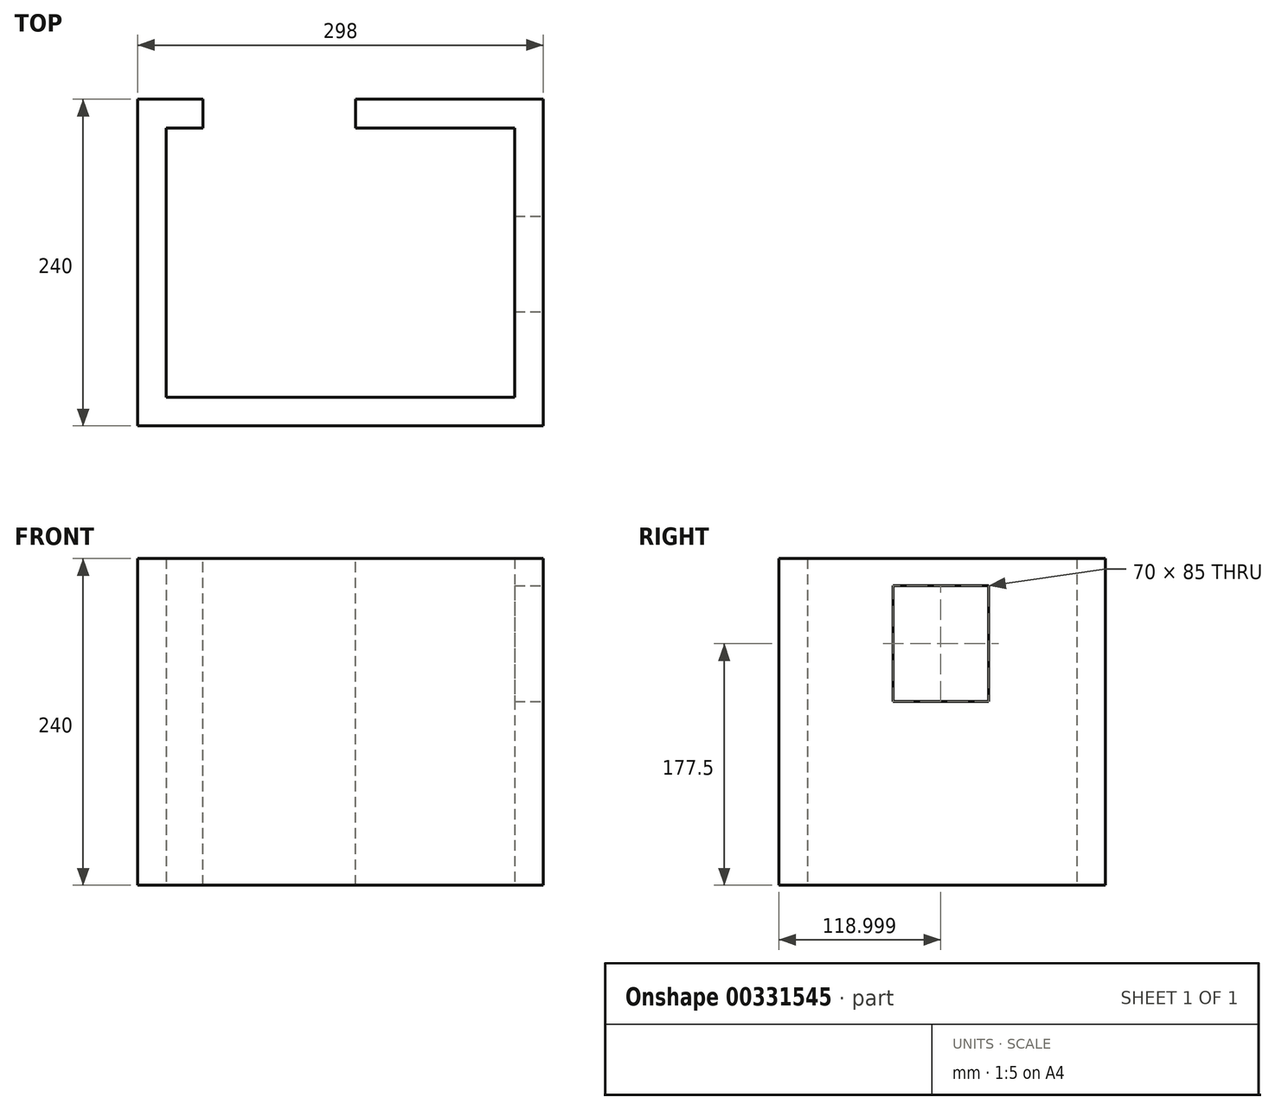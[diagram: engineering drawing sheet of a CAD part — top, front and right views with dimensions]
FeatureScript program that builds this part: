
annotation { "Feature Type Name" : "Feature", "Feature Type Description" : "" }
export const myFeature = defineFeature(function(context is Context, id is Id, definition is map)
    precondition{}
    {
        {
            var Q0;
            Q0=qCreatedBy(makeId("Top.planeOp"),FACE);
            var sketch = newSketch(context, id + "F0", { "sketchPlane" : qUnion([Q0])});
            skLineSegment(sketch, "E0", {"start": v(1313, 440) * mm, "end": v(1313, 406) * mm});
            skLineSegment(sketch, "E1", {"start": v(1313, -267) * mm, "end": v(1313, -301) * mm});
            skLineSegment(sketch, "E2", {"start": v(1313, -301) * mm, "end": v(647, -301) * mm});
            skLineSegment(sketch, "E3", {"start": v(1279, -267) * mm, "end": v(647, -267) * mm});
            skLineSegment(sketch, "E4", {"start": v(1279, 406) * mm, "end": v(688, 406) * mm});
            skLineSegment(sketch, "E5", {"start": v(688, 406) * mm, "end": v(688, -75) * mm});
            skLineSegment(sketch, "E6", {"start": v(688, -75) * mm, "end": v(413, -75) * mm});
            skLineSegment(sketch, "E7", {"start": v(647, -301) * mm, "end": v(647, -267) * mm});
            skLineSegment(sketch, "E8", {"start": v(536, -301) * mm, "end": v(536, -267) * mm});
            skLineSegment(sketch, "E9", {"start": v(536, -267) * mm, "end": v(328, -267) * mm});
            skLineSegment(sketch, "E10", {"start": v(328, -267) * mm, "end": v(328, -407) * mm});
            skLineSegment(sketch, "E11", {"start": v(328, -407) * mm, "end": v(-40, -407) * mm});
            skLineSegment(sketch, "E12", {"start": v(-40, -407) * mm, "end": v(-40, -188) * mm});
            skLineSegment(sketch, "E13", {"start": v(-40, -188) * mm, "end": v(-105, -188) * mm});
            skLineSegment(sketch, "E14", {"start": v(536, -301) * mm, "end": v(362, -301) * mm});
            skLineSegment(sketch, "E15", {"start": v(362, -301) * mm, "end": v(362, -440) * mm});
            skLineSegment(sketch, "E16", {"start": v(-60, -407) * mm, "end": v(-60, -215) * mm});
            skLineSegment(sketch, "E17", {"start": v(-60, -215) * mm, "end": v(-105, -215) * mm});
            skLineSegment(sketch, "E18", {"start": v(-105, -188) * mm, "end": v(-105, -215) * mm});
            skLineSegment(sketch, "E19", {"start": v(-60, -407) * mm, "end": v(-282, -407) * mm});
            skLineSegment(sketch, "E20", {"start": v(-282, -407) * mm, "end": v(-282, -287) * mm});
            skLineSegment(sketch, "E21", {"start": v(-282, -287) * mm, "end": v(-330, -287) * mm});
            skLineSegment(sketch, "E22", {"start": v(-330, -287) * mm, "end": v(-330, -407) * mm});
            skLineSegment(sketch, "E23", {"start": v(-330, -407) * mm, "end": v(-497, -407) * mm});
            skLineSegment(sketch, "E24", {"start": v(-197, -188) * mm, "end": v(-197, -215) * mm});
            skLineSegment(sketch, "E25", {"start": v(-197, -188) * mm, "end": v(-765, -188) * mm});
            skLineSegment(sketch, "E26", {"start": v(-197, -215) * mm, "end": v(-497, -215) * mm});
            skLineSegment(sketch, "E27", {"start": v(-497, -215) * mm, "end": v(-497, -231) * mm});
            skLineSegment(sketch, "E28", {"start": v(-497, -231) * mm, "end": v(-497, -293) * mm});
            skLineSegment(sketch, "E29", {"start": v(-497, -407) * mm, "end": v(-497, -349) * mm});
            skLineSegment(sketch, "E30", {"start": v(413, -75) * mm, "end": v(413, -54) * mm});
            skLineSegment(sketch, "E31", {"start": v(413, -54) * mm, "end": v(667, -54) * mm});
            skLineSegment(sketch, "E32", {"start": v(667, -54) * mm, "end": v(667, 406) * mm});
            skLineSegment(sketch, "E33", {"start": v(667, 406) * mm, "end": v(495, 406) * mm});
            skLineSegment(sketch, "E34", {"start": v(312, 406) * mm, "end": v(391, 406) * mm});
            skLineSegment(sketch, "E35", {"start": v(391, 406) * mm, "end": v(391, 440) * mm});
            skLineSegment(sketch, "E36", {"start": v(495, 406) * mm, "end": v(495, 440) * mm});
            skLineSegment(sketch, "E37", {"start": v(1313, 440) * mm, "end": v(495, 440) * mm});
            skLineSegment(sketch, "E38", {"start": v(312, -75) * mm, "end": v(60, -75) * mm});
            skLineSegment(sketch, "E39", {"start": v(-1279, 406) * mm, "end": v(-1279, 7) * mm});
            skLineSegment(sketch, "E40", {"start": v(-790, 406) * mm, "end": v(-790, 7) * mm});
            skLineSegment(sketch, "E41", {"start": v(-1279, 7) * mm, "end": v(-910, 7) * mm});
            skLineSegment(sketch, "E42", {"start": v(-790, 7) * mm, "end": v(-808, 7) * mm});
            skLineSegment(sketch, "E43", {"start": v(-765, -188) * mm, "end": v(-765, -208) * mm});
            skLineSegment(sketch, "E44", {"start": v(290, 141) * mm, "end": v(290, 406) * mm});
            skLineSegment(sketch, "E45", {"start": v(290, 141) * mm, "end": v(75, 141) * mm});
            skLineSegment(sketch, "E46", {"start": v(75, -46) * mm, "end": v(75, 141) * mm});
            skLineSegment(sketch, "E47", {"start": v(60, -75) * mm, "end": v(60, -46) * mm});
            skLineSegment(sketch, "E48", {"start": v(391, 406) * mm, "end": v(312, 406) * mm});
            skLineSegment(sketch, "E49", {"start": v(-139, 406) * mm, "end": v(-139, 440) * mm});
            skLineSegment(sketch, "E50", {"start": v(-318, 406) * mm, "end": v(-318, 440) * mm});
            skLineSegment(sketch, "E51", {"start": v(-515, 406) * mm, "end": v(-515, 440) * mm});
            skLineSegment(sketch, "E52", {"start": v(-694, 406) * mm, "end": v(-694, 440) * mm});
            skLineSegment(sketch, "E53", {"start": v(-770, 406) * mm, "end": v(-770, 9) * mm});
            skLineSegment(sketch, "E54", {"start": v(-694, 406) * mm, "end": v(-770, 406) * mm});
            skLineSegment(sketch, "E55", {"start": v(75, 406) * mm, "end": v(-139, 406) * mm});
            skLineSegment(sketch, "E56", {"start": v(-318, 406) * mm, "end": v(-515, 406) * mm});
            skLineSegment(sketch, "E57", {"start": v(-318, 440) * mm, "end": v(-515, 440) * mm});
            skLineSegment(sketch, "E58", {"start": v(-770, 9) * mm, "end": v(-754, 9) * mm});
            skLineSegment(sketch, "E59", {"start": v(-677, 9) * mm, "end": v(-659, 9) * mm});
            skLineSegment(sketch, "E60", {"start": v(-659, 9) * mm, "end": v(-659, -5) * mm});
            skLineSegment(sketch, "E61", {"start": v(-659, -5) * mm, "end": v(-659, -46) * mm});
            skLineSegment(sketch, "E62", {"start": v(-659, -46) * mm, "end": v(-60, -46) * mm});
            skLineSegment(sketch, "E63", {"start": v(-60, -75) * mm, "end": v(-60, -46) * mm});
            skLineSegment(sketch, "E64", {"start": v(60, -75) * mm, "end": v(128, -75) * mm});
            skLineSegment(sketch, "E65", {"start": v(60, -46) * mm, "end": v(75, -46) * mm});
            skLineSegment(sketch, "E66", {"start": v(96, -46) * mm, "end": v(290, -46) * mm});
            skLineSegment(sketch, "E67", {"start": v(-60, -75) * mm, "end": v(-677, -75) * mm});
            skLineSegment(sketch, "E68", {"start": v(-677, 9) * mm, "end": v(-677, -75) * mm});
            skLineSegment(sketch, "E69", {"start": v(-754, 9) * mm, "end": v(-754, -13) * mm});
            skLineSegment(sketch, "E70", {"start": v(-808, 7) * mm, "end": v(-808, -13) * mm});
            skLineSegment(sketch, "E71", {"start": v(-808, -13) * mm, "end": v(-754, -13) * mm});
            skLineSegment(sketch, "E72", {"start": v(-910, 7) * mm, "end": v(-910, -29) * mm});
            skLineSegment(sketch, "E73", {"start": v(-1279, -406) * mm, "end": v(-935, -406) * mm});
            skLineSegment(sketch, "E74", {"start": v(-1313, -440) * mm, "end": v(-935, -440) * mm});
            skLineSegment(sketch, "E75", {"start": v(-910, -29) * mm, "end": v(-935, -29) * mm});
            skLineSegment(sketch, "E76", {"start": v(-935, -13) * mm, "end": v(-1279, -13) * mm});
            skLineSegment(sketch, "E77", {"start": v(-910, -132) * mm, "end": v(-935, -132) * mm});
            skLineSegment(sketch, "E78", {"start": v(-910, -29) * mm, "end": v(-910, -13) * mm});
            skLineSegment(sketch, "E79", {"start": v(-935, -406) * mm, "end": v(-935, -132) * mm});
            skLineSegment(sketch, "E80", {"start": v(-935, -29) * mm, "end": v(-935, -13) * mm});
            skLineSegment(sketch, "E81", {"start": v(-877, -208) * mm, "end": v(-877, -188) * mm});
            skLineSegment(sketch, "E82", {"start": v(-910, -132) * mm, "end": v(-910, -188) * mm});
            skLineSegment(sketch, "E83", {"start": v(-877, -188) * mm, "end": v(-910, -188) * mm});
            skLineSegment(sketch, "E84", {"start": v(-877, -208) * mm, "end": v(-904, -208) * mm});
            skLineSegment(sketch, "E85", {"start": v(-904, -208) * mm, "end": v(-904, -406) * mm});
            skLineSegment(sketch, "E86", {"start": v(-904, -406) * mm, "end": v(-648, -406) * mm});
            skLineSegment(sketch, "E87", {"start": v(-765, -208) * mm, "end": v(-648, -208) * mm});
            skLineSegment(sketch, "E88", {"start": v(-648, -208) * mm, "end": v(-648, -273) * mm});
            skLineSegment(sketch, "E89", {"start": v(-648, -406) * mm, "end": v(-648, -343) * mm});
            skLineSegment(sketch, "E90", {"start": v(-935, -440) * mm, "end": v(362, -440) * mm});
            skLineSegment(sketch, "E91", {"start": v(151, 406) * mm, "end": v(151, 440) * mm});
            skLineSegment(sketch, "E92", {"start": v(224, 406) * mm, "end": v(224, 440) * mm});
            skLineSegment(sketch, "E93", {"start": v(290, 406) * mm, "end": v(224, 406) * mm});
            skLineSegment(sketch, "E94", {"start": v(151, 406) * mm, "end": v(96, 406) * mm});
            skLineSegment(sketch, "E95", {"start": v(391, 440) * mm, "end": v(224, 440) * mm});
            skLineSegment(sketch, "E96", {"start": v(151, 440) * mm, "end": v(-139, 440) * mm});
            skLineSegment(sketch, "E97", {"start": v(-907, 406) * mm, "end": v(-907, 440) * mm});
            skLineSegment(sketch, "E98", {"start": v(-1085, 406) * mm, "end": v(-1085, 440) * mm});
            skLineSegment(sketch, "E99", {"start": v(-790, 406) * mm, "end": v(-907, 406) * mm});
            skLineSegment(sketch, "E100", {"start": v(-1085, 406) * mm, "end": v(-1279, 406) * mm});
            skLineSegment(sketch, "E101", {"start": v(-694, 440) * mm, "end": v(-907, 440) * mm});
            skLineSegment(sketch, "E102", {"start": v(-1085, 440) * mm, "end": v(-1313, 440) * mm});
            skLineSegment(sketch, "E103", {"start": v(-1279, -118) * mm, "end": v(-1313, -118) * mm});
            skLineSegment(sketch, "E104", {"start": v(-1279, -297) * mm, "end": v(-1313, -297) * mm});
            skLineSegment(sketch, "E105", {"start": v(-1279, -13) * mm, "end": v(-1279, -118) * mm});
            skLineSegment(sketch, "E106", {"start": v(-1279, -297) * mm, "end": v(-1279, -406) * mm});
            skLineSegment(sketch, "E107", {"start": v(-1313, 440) * mm, "end": v(-1313, -118) * mm});
            skLineSegment(sketch, "E108", {"start": v(-1313, -297) * mm, "end": v(-1313, -440) * mm});
            skLineSegment(sketch, "E109", {"start": v(-648, -273) * mm, "end": v(-630, -273) * mm});
            skLineSegment(sketch, "E110", {"start": v(-648, -343) * mm, "end": v(-630, -343) * mm});
            skLineSegment(sketch, "E111", {"start": v(-515, -349) * mm, "end": v(-497, -349) * mm});
            skLineSegment(sketch, "E112", {"start": v(-515, -293) * mm, "end": v(-497, -293) * mm});
            skLineSegment(sketch, "E113", {"start": v(-515, -349) * mm, "end": v(-515, -406) * mm});
            skLineSegment(sketch, "E114", {"start": v(-630, -343) * mm, "end": v(-630, -406) * mm});
            skLineSegment(sketch, "E115", {"start": v(-630, -406) * mm, "end": v(-515, -406) * mm});
            skLineSegment(sketch, "E116", {"start": v(-630, -273) * mm, "end": v(-630, -206) * mm});
            skLineSegment(sketch, "E117", {"start": v(-630, -206) * mm, "end": v(-515, -206) * mm});
            skLineSegment(sketch, "E118", {"start": v(-515, -293) * mm, "end": v(-515, -206) * mm});
            skLineSegment(sketch, "E119", {"start": v(290, 43) * mm, "end": v(312, 43) * mm});
            skLineSegment(sketch, "E120", {"start": v(290, 124) * mm, "end": v(312, 124) * mm});
            skLineSegment(sketch, "E121", {"start": v(312, -75) * mm, "end": v(312, 43) * mm});
            skLineSegment(sketch, "E122", {"start": v(312, 124) * mm, "end": v(312, 406) * mm});
            skLineSegment(sketch, "E123", {"start": v(290, -46) * mm, "end": v(290, 43) * mm});
            skLineSegment(sketch, "E124", {"start": v(96, 222) * mm, "end": v(75, 222) * mm});
            skLineSegment(sketch, "E125", {"start": v(96, 222) * mm, "end": v(96, 406) * mm});
            skLineSegment(sketch, "E126", {"start": v(75, 222) * mm, "end": v(75, 406) * mm});
            skLineSegment(sketch, "E127", {"start": v(96, -46) * mm, "end": v(96, 124) * mm});
            skLineSegment(sketch, "E128", {"start": v(290, 124) * mm, "end": v(96, 124) * mm});
            skLineSegment(sketch, "E129", {"start": v(1279, -219) * mm, "end": v(1313, -219) * mm});
            skLineSegment(sketch, "E130", {"start": v(1279, -26) * mm, "end": v(1313, -26) * mm});
            skLineSegment(sketch, "E131", {"start": v(1279, 46) * mm, "end": v(1313, 46) * mm});
            skLineSegment(sketch, "E132", {"start": v(1279, 239) * mm, "end": v(1313, 239) * mm});
            skLineSegment(sketch, "E133", {"start": v(1313, 406) * mm, "end": v(1313, 239) * mm});
            skLineSegment(sketch, "E134", {"start": v(1279, 406) * mm, "end": v(1279, 239) * mm});
            skLineSegment(sketch, "E135", {"start": v(1313, 46) * mm, "end": v(1313, -26) * mm});
            skLineSegment(sketch, "E136", {"start": v(1313, -219) * mm, "end": v(1313, -267) * mm});
            skLineSegment(sketch, "E137", {"start": v(1279, 46) * mm, "end": v(1279, -26) * mm});
            skLineSegment(sketch, "E138", {"start": v(1279, -219) * mm, "end": v(1279, -267) * mm});
            skLineSegment(sketch, "E139", {"start": v(1313, -301) * mm, "end": v(1313, 440) * mm});
            skLineSegment(sketch, "E140", {"start": v(1313, -301) * mm, "end": v(362, -301) * mm});
            skLineSegment(sketch, "E141", {"start": v(362, -440) * mm, "end": v(-1313, -440) * mm});
            skLineSegment(sketch, "E142", {"start": v(-1313, 440) * mm, "end": v(-1313, -440) * mm});
            skLineSegment(sketch, "E143", {"start": v(-1313, 440) * mm, "end": v(1313, 440) * mm});
            skLineSegment(sketch, "E144", {"start": v(-321.5, -37.21) * mm, "end": v(-321.5, 162.79) * mm});
            skLineSegment(sketch, "E145", {"start": v(-321.5, -37.21) * mm, "end": v(-511.5, -37.21) * mm});
            skLineSegment(sketch, "E146", {"start": v(-321.5, 162.79) * mm, "end": v(-511.5, 162.79) * mm});
            skLineSegment(sketch, "E147", {"start": v(-511.5, -37.21) * mm, "end": v(-511.5, 162.79) * mm});
            skLineSegment(sketch, "E148", {"start": v(-321.5, -29.2) * mm, "end": v(-511.5, -29.2) * mm});
            skLineSegment(sketch, "E149", {"start": v(-499.08, -21.75) * mm, "end": v(-430.85, -21.75) * mm});
            skLineSegment(sketch, "E150", {"start": v(-430.85, -21.75) * mm, "end": v(-430.85, 2.94) * mm});
            skLineSegment(sketch, "E151", {"start": v(-430.85, 2.94) * mm, "end": v(-499.08, 2.94) * mm});
            skLineSegment(sketch, "E152", {"start": v(-499.08, 2.94) * mm, "end": v(-499.08, -21.75) * mm});
            skLineSegment(sketch, "E153", {"start": v(-333.92, -21.75) * mm, "end": v(-402.15, -21.75) * mm});
            skLineSegment(sketch, "E154", {"start": v(-402.15, -21.75) * mm, "end": v(-402.15, 2.94) * mm});
            skLineSegment(sketch, "E155", {"start": v(-402.15, 2.94) * mm, "end": v(-333.92, 2.94) * mm});
            skLineSegment(sketch, "E156", {"start": v(-333.92, 2.94) * mm, "end": v(-333.92, -21.75) * mm});
            skLineSegment(sketch, "E157", {"start": v(-321.5, 13.1) * mm, "end": v(-416.5, 13.1) * mm});
            skLineSegment(sketch, "E158", {"start": v(-511.5, 36.6) * mm, "end": v(-491.94, 63.04) * mm});
            skLineSegment(sketch, "E159", {"start": v(-491.94, 63.04) * mm, "end": v(-416.5, 13.1) * mm});
            skLineSegment(sketch, "E160", {"start": v(-416.5, 13.1) * mm, "end": v(-511.5, 36.6) * mm});
            skLineSegment(sketch, "E161", {"start": v(-321.5, 159.23) * mm, "end": v(-511.5, 159.23) * mm});
            skLineSegment(sketch, "E162", {"start": v(-552.43, 3.31) * mm, "end": v(-520.43, 3.31) * mm});
            skLineSegment(sketch, "E163", {"start": v(-552.43, 3.31) * mm, "end": v(-552.43, -36.7) * mm});
            skLineSegment(sketch, "E164", {"start": v(-520.43, 3.31) * mm, "end": v(-520.43, -36.7) * mm});
            skLineSegment(sketch, "E165", {"start": v(-552.43, -36.7) * mm, "end": v(-520.43, -36.7) * mm});
            skLineSegment(sketch, "E166", {"start": v(-552.43, -6.69) * mm, "end": v(-520.43, -6.69) * mm});
            skLineSegment(sketch, "E167", {"start": v(-552.43, -3.69) * mm, "end": v(-520.43, -3.69) * mm});
            skLineSegment(sketch, "E168", {"start": v(-552.43, -0.69) * mm, "end": v(-520.43, -0.69) * mm});
            skLineSegment(sketch, "E169", {"start": v(-552.43, 2.31) * mm, "end": v(-520.43, 2.31) * mm});
            skLineSegment(sketch, "E170", {"start": v(-280.57, 3.31) * mm, "end": v(-312.57, 3.31) * mm});
            skLineSegment(sketch, "E171", {"start": v(-280.57, 3.31) * mm, "end": v(-280.57, -36.7) * mm});
            skLineSegment(sketch, "E172", {"start": v(-312.57, 3.31) * mm, "end": v(-312.57, -36.7) * mm});
            skLineSegment(sketch, "E173", {"start": v(-280.57, -36.7) * mm, "end": v(-312.57, -36.7) * mm});
            skLineSegment(sketch, "E174", {"start": v(-280.57, -6.69) * mm, "end": v(-312.57, -6.69) * mm});
            skLineSegment(sketch, "E175", {"start": v(-280.57, -3.69) * mm, "end": v(-312.57, -3.69) * mm});
            skLineSegment(sketch, "E176", {"start": v(-280.57, -0.69) * mm, "end": v(-312.57, -0.69) * mm});
            skLineSegment(sketch, "E177", {"start": v(-280.57, 2.31) * mm, "end": v(-312.57, 2.31) * mm});
            skLineSegment(sketch, "E178", {"start": v(-765, 395.6) * mm, "end": v(-765, 20.6) * mm});
            skLineSegment(sketch, "E179", {"start": v(-765, 395.6) * mm, "end": v(-705, 395.6) * mm});
            skLineSegment(sketch, "E180", {"start": v(-705, 395.6) * mm, "end": v(-705, 20.6) * mm});
            skLineSegment(sketch, "E181", {"start": v(-765, 20.6) * mm, "end": v(-705, 20.6) * mm});
            skLineSegment(sketch, "E182", {"start": v(-705, 395.6) * mm, "end": v(-700, 395.6) * mm});
            skLineSegment(sketch, "E183", {"start": v(-700, 395.6) * mm, "end": v(-700, 20.6) * mm});
            skLineSegment(sketch, "E184", {"start": v(-705, 20.6) * mm, "end": v(-700, 20.6) * mm});
            skLineSegment(sketch, "E185", {"start": v(-705, 114.35) * mm, "end": v(-700, 114.35) * mm});
            skLineSegment(sketch, "E186", {"start": v(-705, 301.85) * mm, "end": v(-700, 301.85) * mm});
            skLineSegment(sketch, "E187", {"start": v(-705, 208.1) * mm, "end": v(-700, 208.1) * mm});
            skLineSegment(sketch, "E188", {"start": v(-705, 348.73) * mm, "end": v(-700, 348.73) * mm});
            skLineSegment(sketch, "E189", {"start": v(-705, 67.47) * mm, "end": v(-700, 67.47) * mm});
            skSolve(sketch);
        }
        {
            var Q0;
            Q0=makeQuery(id+"F0.imprint","IMPRINT",FACE,{"disambiguationData":[TD([[makeQuery(id+"F0.imprint","IMPRINT",EDGE,{"derivedFrom":sQuery(id+"F0.wireOp",EDGE,"E3")}),-1.0]])]});
            var sketch = newSketch(context, id + "F1", { "sketchPlane" : qUnion([Q0])});
            skLineSegment(sketch, "E190.0", {"start": v(-904, -208) * mm, "end": v(-904, -406) * mm});
            skLineSegment(sketch, "E191.0", {"start": v(-904, -406) * mm, "end": v(-648, -406) * mm});
            skLineSegment(sketch, "E192.0", {"start": v(-648, -208) * mm, "end": v(-648, -273) * mm});
            skLineSegment(sketch, "E193.0", {"start": v(-648, -406) * mm, "end": v(-648, -343) * mm});
            skLineSegment(sketch, "E194.0", {"start": v(-765, -208) * mm, "end": v(-648, -208) * mm});
            skLineSegment(sketch, "E195", {"start": v(-648, -273) * mm, "end": v(-648, -343) * mm});
            skLineSegment(sketch, "E196", {"start": v(-765, -208) * mm, "end": v(-904, -208) * mm});
            skSolve(sketch);
        }
        {
            var Q0;
            {var subQ0=sQuery(id+"F1.wireOp",EDGE,"E190.0");Q0=makeQuery(id+"F1.imprint","IMPRINT",FACE,{"disambiguationData":[TD([[makeQuery(id+"F1.imprint","IMPRINT",EDGE,{"derivedFrom":subQ0}),1.0]])]});}
            var sketch = newSketch(context, id + "F2", { "sketchPlane" : qUnion([Q0])});
            skLineSegment(sketch, "E197.0", {"start": v(-627, -273) * mm, "end": v(-627, -187) * mm});
            skLineSegment(sketch, "E197.1", {"start": v(-627, -343) * mm, "end": v(-627, -273) * mm});
            skLineSegment(sketch, "E197.2", {"start": v(-627, -187) * mm, "end": v(-765, -187) * mm});
            skLineSegment(sketch, "E197.3", {"start": v(-627, -427) * mm, "end": v(-627, -343) * mm});
            skLineSegment(sketch, "E197.4", {"start": v(-765, -187) * mm, "end": v(-877, -187) * mm});
            skLineSegment(sketch, "E197.5", {"start": v(-877, -187) * mm, "end": v(-925, -187) * mm});
            skLineSegment(sketch, "E197.6", {"start": v(-925, -187) * mm, "end": v(-925, -427) * mm});
            skLineSegment(sketch, "E197.7", {"start": v(-925, -427) * mm, "end": v(-627, -427) * mm});
            skLineSegment(sketch, "E198.0.0", {"start": v(-648, -208) * mm, "end": v(-765, -208) * mm});
            skLineSegment(sketch, "E198.0.1", {"start": v(-765, -208) * mm, "end": v(-877, -208) * mm});
            skLineSegment(sketch, "E198.0.2", {"start": v(-877, -208) * mm, "end": v(-904, -208) * mm});
            skLineSegment(sketch, "E198.0.3", {"start": v(-904, -208) * mm, "end": v(-904, -406) * mm});
            skLineSegment(sketch, "E198.0.4", {"start": v(-904, -406) * mm, "end": v(-648, -406) * mm});
            skLineSegment(sketch, "E198.0.5", {"start": v(-648, -406) * mm, "end": v(-648, -343) * mm});
            skLineSegment(sketch, "E198.0.6", {"start": v(-648, -343) * mm, "end": v(-648, -273) * mm});
            skLineSegment(sketch, "E198.0.7", {"start": v(-648, -273) * mm, "end": v(-648, -208) * mm});
            skSolve(sketch);
        }
        {
            var Q0;
            Q0=qSketchRegion(id+"F2",true);
            extrude(context, id + "F3", {"entities" : qUnion([Q0]), "depth" : (220 + 20) * mm});
        }
        {
            var Q0;
            {var subQ0=sQuery(id+"F1.wireOp",EDGE,"E190.0");Q0=makeQuery(id+"F1.imprint","IMPRINT",FACE,{"disambiguationData":[TD([[makeQuery(id+"F1.imprint","IMPRINT",EDGE,{"derivedFrom":subQ0}),1.0]])]});}
            var sketch = newSketch(context, id + "F4", { "sketchPlane" : qUnion([Q0])});
            skLineSegment(sketch, "E199.0.0", {"start": v(-648, -208) * mm, "end": v(-765, -208) * mm});
            skLineSegment(sketch, "E199.0.1", {"start": v(-765, -208) * mm, "end": v(-877, -208) * mm});
            skLineSegment(sketch, "E199.0.2", {"start": v(-877, -208) * mm, "end": v(-904, -208) * mm});
            skLineSegment(sketch, "E199.0.3", {"start": v(-904, -208) * mm, "end": v(-904, -406) * mm});
            skLineSegment(sketch, "E199.0.4", {"start": v(-904, -406) * mm, "end": v(-648, -406) * mm});
            skLineSegment(sketch, "E199.0.5", {"start": v(-648, -406) * mm, "end": v(-648, -343) * mm});
            skLineSegment(sketch, "E199.0.6", {"start": v(-648, -343) * mm, "end": v(-648, -273) * mm});
            skLineSegment(sketch, "E199.0.7", {"start": v(-648, -273) * mm, "end": v(-648, -208) * mm});
            skSolve(sketch);
        }
        {
            var Q0;
            Q0=qSketchRegion(id+"F4",true);
            extrude(context, id + "F5", {"entities" : qUnion([Q0]), "operationType" : NewBodyOperationType.ADD, "depth" : 20 * mm});
        }
        {
            var Q0;
            Q0=makeQuery(id+"F3.opExtrude","SWEPT_FACE",FACE,{"disambiguationData":[OSD([sQuery(id+"F2.wireOp",EDGE,"E197.2"),sQuery(id+"F2.wireOp",EDGE,"E197.4"),sQuery(id+"F2.wireOp",EDGE,"E197.5")])]});
            var sketch = newSketch(context, id + "F6", { "sketchPlane" : qUnion([Q0])});
            skLineSegment(sketch, "E200.0", {"start": v(904, 240) * mm, "end": v(904, 20) * mm});
            skLineSegment(sketch, "E201.0", {"start": v(877, 0) * mm, "end": v(910, 0) * mm});
            skLineSegment(sketch, "E202.0", {"start": v(197, 0) * mm, "end": v(765, 0) * mm});
            skLineSegment(sketch, "E203", {"start": v(877, 20) * mm, "end": v(877, 261.1) * mm});
            skLineSegment(sketch, "E204", {"start": v(877, 261.1) * mm, "end": v(765, 261.1) * mm});
            skLineSegment(sketch, "E205", {"start": v(765, 261.1) * mm, "end": v(765, 20) * mm});
            skLineSegment(sketch, "E206", {"start": v(765, 20) * mm, "end": v(877, 20) * mm});
            skSolve(sketch);
        }
        {
            var Q0;
            Q0=qSketchRegion(id+"F6",true);
            extrude(context, id + "F7", {"entities" : qUnion([Q0]), "operationType" : NewBodyOperationType.REMOVE, "oppositeDirection" : true, "depth" : 25 * mm});
        }
        {
            var Q0;
            Q0=makeQuery(id+"F3.opExtrude","SWEPT_FACE",FACE,{"disambiguationData":[OSD([sQuery(id+"F2.wireOp",EDGE,"E197.0"),sQuery(id+"F2.wireOp",EDGE,"E197.1"),sQuery(id+"F2.wireOp",EDGE,"E197.3")])]});
            var sketch = newSketch(context, id + "F8", { "sketchPlane" : qUnion([Q0])});
            skLineSegment(sketch, "E207.0", {"start": v(-208, 0) * mm, "end": v(-273, 0) * mm, "construction": true});
            skLineSegment(sketch, "E208.0", {"start": v(-406, 0) * mm, "end": v(-343, 0) * mm, "construction": true});
            skLineSegment(sketch, "E209.0", {"start": v(-406, 20) * mm, "end": v(-208, 20) * mm, "construction": true});
            skLineSegment(sketch, "E210", {"start": v(-273, 135) * mm, "end": v(-343, 135) * mm});
            skLineSegment(sketch, "E211", {"start": v(-343, 135) * mm, "end": v(-343, 220) * mm});
            skLineSegment(sketch, "E212", {"start": v(-343, 220) * mm, "end": v(-273, 220) * mm});
            skLineSegment(sketch, "E213", {"start": v(-273, 220) * mm, "end": v(-273, 135) * mm});
            skSolve(sketch);
        }
        {
            var Q0;
            Q0=qSketchRegion(id+"F8",true);
            extrude(context, id + "F9", {"entities" : qUnion([Q0]), "operationType" : NewBodyOperationType.REMOVE, "oppositeDirection" : true, "depth" : 25 * mm});
        }
        {
            var Q0;
            Q0=makeQuery(id+"F7.boolean.opBoolean","MERGE",FACE,{"derivedFrom":[makeQuery(id+"F5.opExtrude","CAP_FACE",FACE,{"disambiguationData":[OSD([sQuery(id+"F4.wireOp",EDGE,"E199.0.0"),sQuery(id+"F4.wireOp",EDGE,"E199.0.1"),sQuery(id+"F4.wireOp",EDGE,"E199.0.2"),sQuery(id+"F4.wireOp",EDGE,"E199.0.3"),sQuery(id+"F4.wireOp",EDGE,"E199.0.4"),sQuery(id+"F4.wireOp",EDGE,"E199.0.5"),sQuery(id+"F4.wireOp",EDGE,"E199.0.6"),sQuery(id+"F4.wireOp",EDGE,"E199.0.7")])],"isStart":false}),makeQuery(id+"F7.opExtrude","SWEPT_FACE",FACE,{"disambiguationData":[OSD([sQuery(id+"F6.wireOp",EDGE,"E206")])]})]});
            var sketch = newSketch(context, id + "F10", { "sketchPlane" : qUnion([Q0])});
            skLineSegment(sketch, "E214.0", {"start": v(-648, -406) * mm, "end": v(-648, -208) * mm});
            skLineSegment(sketch, "E215", {"start": v(-648, -208) * mm, "end": v(-698, -208) * mm});
            skLineSegment(sketch, "E216", {"start": v(-698, -208) * mm, "end": v(-698, -406) * mm});
            skLineSegment(sketch, "E217", {"start": v(-698, -406) * mm, "end": v(-648, -406) * mm});
            skSolve(sketch);
        }
        {
            var Q0;
            Q0=qSketchRegion(id+"F10",true);
            extrude(context, id + "F11", {"entities" : qUnion([Q0]), "operationType" : NewBodyOperationType.ADD, "depth" : 50 * mm});
        }
        {
            var Q0;
            Q0=makeQuery(id+"F7.boolean.opBoolean","MERGE",FACE,{"derivedFrom":[makeQuery(id+"F5.opExtrude","CAP_FACE",FACE,{"disambiguationData":[OSD([sQuery(id+"F4.wireOp",EDGE,"E199.0.0"),sQuery(id+"F4.wireOp",EDGE,"E199.0.1"),sQuery(id+"F4.wireOp",EDGE,"E199.0.2"),sQuery(id+"F4.wireOp",EDGE,"E199.0.3"),sQuery(id+"F4.wireOp",EDGE,"E199.0.4"),sQuery(id+"F4.wireOp",EDGE,"E199.0.5"),sQuery(id+"F4.wireOp",EDGE,"E199.0.6"),sQuery(id+"F4.wireOp",EDGE,"E199.0.7")])],"isStart":false}),makeQuery(id+"F7.opExtrude","SWEPT_FACE",FACE,{"disambiguationData":[OSD([sQuery(id+"F6.wireOp",EDGE,"E206")])]})]});
            extrude(context, id + "F12", {"entities" : qUnion([Q0]), "operationType" : NewBodyOperationType.REMOVE, "oppositeDirection" : true, "depth" : 25 * mm});
        }
        {
            var Q0;
            Q0=makeQuery(id+"F11.opExtrude","CAP_FACE",FACE,{"disambiguationData":[OSD([sQuery(id+"F10.wireOp",EDGE,"E214.0"),sQuery(id+"F10.wireOp",EDGE,"E215"),sQuery(id+"F10.wireOp",EDGE,"E216"),sQuery(id+"F10.wireOp",EDGE,"E217")])],"isStart":false});
            extrude(context, id + "F13", {"entities" : qUnion([Q0]), "operationType" : NewBodyOperationType.REMOVE, "endBound" : BoundingType.THROUGH_ALL, "oppositeDirection" : true, "depth" : 25 * mm});
        }
    });
